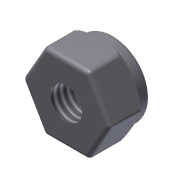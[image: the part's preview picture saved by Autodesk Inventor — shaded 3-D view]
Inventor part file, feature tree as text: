
AUTODESK INVENTOR PART (.ipt)
format: ipt  version: 2013 (Build 170138000, 138)  size: 180,736 bytes
history: native  units: in
note: dims shown in document units (in); Inventor stores cm internally (conversion verified against a paired STEP export)
features: sketch x5, extrude x3, fillet x2, hole x1, revolve x1, projected_geometry x1
ambient origin geometry x8: Origin, YZ Plane, XZ Plane, XY Plane, X Axis, Y Axis, Z Axis, Center Point
bodies: Solid1 (feature_tree)
feature tree (13):
  extrude  "Extrusion1"  Depth=0.1719in TaperAngle=0.0deg
  extrude  "Extrusion2"  Depth=0.0625in TaperAngle=0.0deg
  extrude  "Extrusion3"  Depth=0.01in TaperAngle=0.0deg
  hole  "Hole2"  [1 undecoded]
  revolve  "Revolution2"  [1 undecoded]
  fillet  "Fillet1"  Radius=0.02in
  fillet  "Fillet2"  [1 undecoded]
  sketch  "Sketch1"  dims[d0=0.375in d1=0.1719in d2=0.0in]
  sketch  "Sketch3"  dims[d3=0.36in d4=0.0625in d5=0.0in]
  sketch  "Sketch8"  dims[d14=0.25in d15=0.01in d16=0.0in]
  sketch  "Sketch9"  dims[d17=0.156in d18=0.172in d19=0.375in d20=0.25in d21=0.5635in d22=1.0in d23=0.8108in d24=0.18in]
  sketch  "Sketch10"  dims[d25=90.0deg d26=0.02in d27=0.02in]
  projected_geometry  "Projected Loop8"
note: 3 required parameter values undecoded (feature->parameter linkage not recoverable at this tier; creation-order binding heuristic only, values carry confidence <= 0.55)